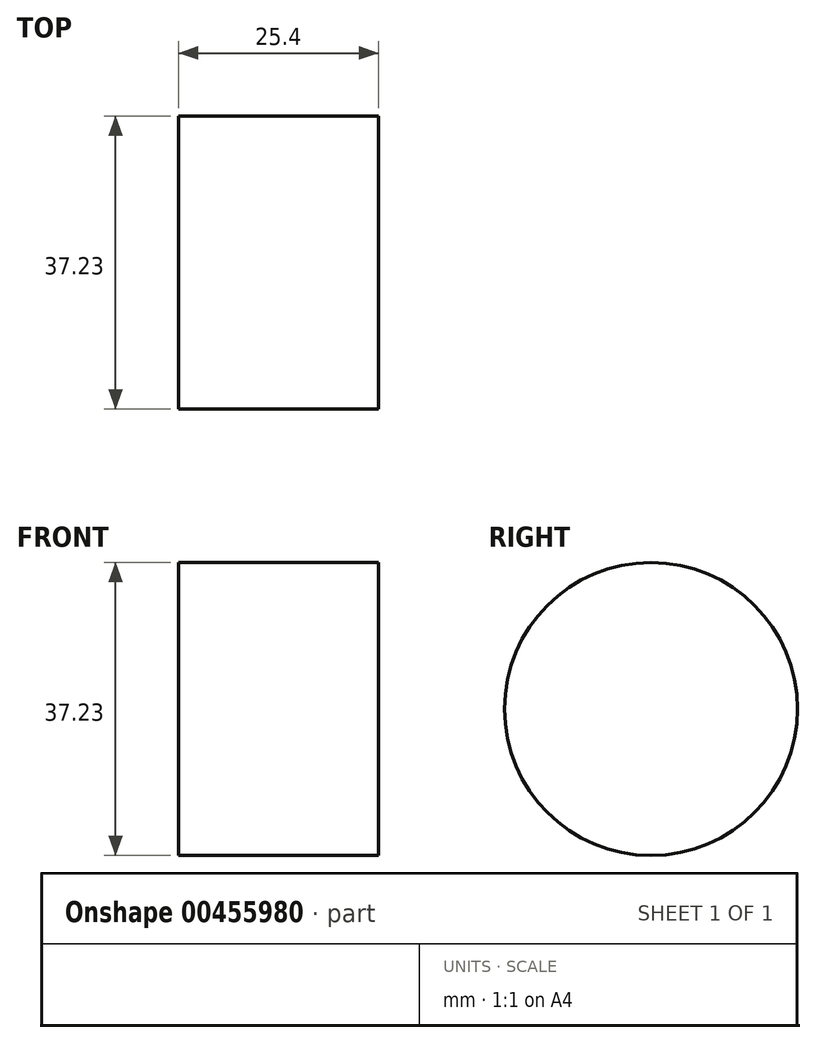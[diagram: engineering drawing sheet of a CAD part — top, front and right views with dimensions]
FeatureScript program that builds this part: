
annotation { "Feature Type Name" : "Feature", "Feature Type Description" : "" }
export const myFeature = defineFeature(function(context is Context, id is Id, definition is map)
    precondition{}
    {
        {
            var Q0;
            Q0=qCreatedBy(makeId("Right.planeOp"),FACE);
            var sketch = newSketch(context, id + "F0", { "sketchPlane" : qUnion([Q0])});
            skCircle(sketch, "E0", {"center": v(-33.25, 29.76) * mm, "radius": 18.61 * mm});
            skPoint(sketch, "E0.first.point", {"position": v(-50.94, 23.96) * mm});
            skPoint(sketch, "E0.second.point", {"position": v(-38.38, 11.86) * mm});
            skPoint(sketch, "E0.third.point", {"position": v(-25.58, 12.8) * mm});
            skSolve(sketch);
        }
        {
            var Q0;
            Q0=makeQuery(id+"F0.imprint","IMPRINT",FACE,{"disambiguationData":[TD([[makeQuery(id+"F0.imprint","IMPRINT",EDGE,{"derivedFrom":sQuery(id+"F0.wireOp",EDGE,"E0")}),1.0]])]});
            extrude(context, id + "F1", {"entities" : qUnion([Q0]), "depth" : 25.4 * mm});
        }
    });
